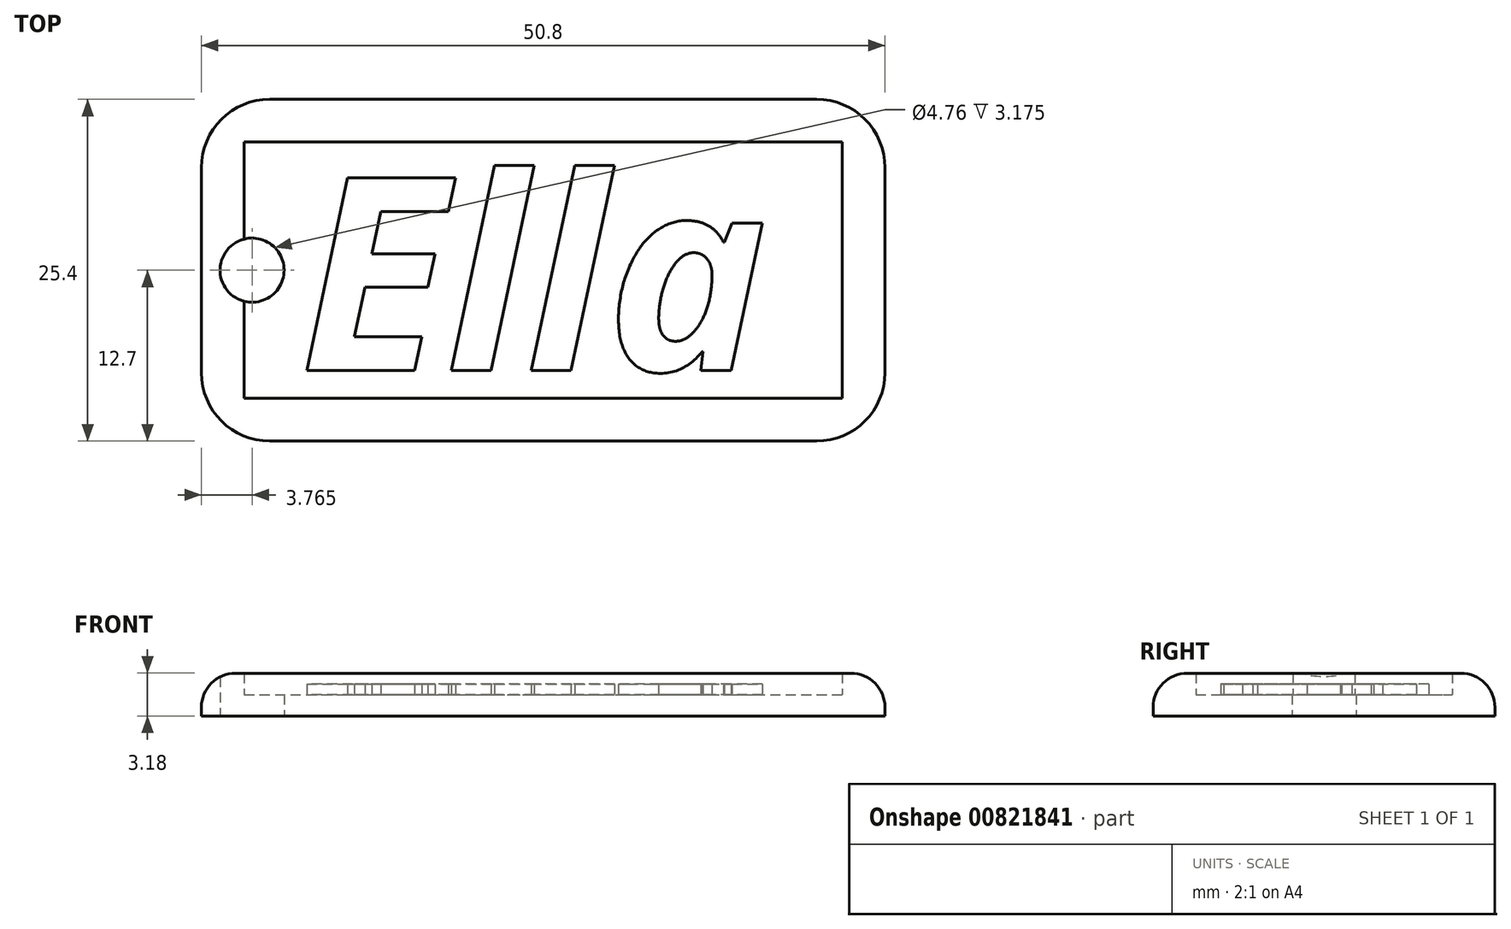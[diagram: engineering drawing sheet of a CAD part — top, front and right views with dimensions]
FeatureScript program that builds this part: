
annotation { "Feature Type Name" : "Feature", "Feature Type Description" : "" }
export const myFeature = defineFeature(function(context is Context, id is Id, definition is map)
    precondition{}
    {
        {
            var Q0;
            Q0=qCreatedBy(makeId("Top.planeOp"),FACE);
            var sketch = newSketch(context, id + "F0", { "sketchPlane" : qUnion([Q0])});
            skLineSegment(sketch, "E0.bottom", {"start": v(0, 0) * mm, "end": v(50.8, 0) * mm});
            skLineSegment(sketch, "E0.top", {"start": v(0, 25.4) * mm, "end": v(50.8, 25.4) * mm});
            skLineSegment(sketch, "E0.left", {"start": v(0, 0) * mm, "end": v(0, 25.4) * mm});
            skLineSegment(sketch, "E0.right", {"start": v(50.8, 0) * mm, "end": v(50.8, 25.4) * mm});
            skCircle(sketch, "E1", {"center": v(3.76, 12.7) * mm, "radius": 2.38 * mm});
            skPoint(sketch, "E1.centerSnap0", {"position": v(0, 12.7) * mm});
            skLineSegment(sketch, "E2.0", {"start": v(3.18, 22.23) * mm, "end": v(47.62, 22.23) * mm});
            skLineSegment(sketch, "E2.1", {"start": v(3.18, 3.18) * mm, "end": v(3.18, 22.22) * mm});
            skLineSegment(sketch, "E2.2", {"start": v(3.18, 3.18) * mm, "end": v(47.62, 3.18) * mm});
            skLineSegment(sketch, "E2.3", {"start": v(47.62, 3.18) * mm, "end": v(47.62, 22.23) * mm});
            skSolve(sketch);
        }
        {
            var Q0;
            {var subQ1=sQuery(id+"F0.wireOp",EDGE,"E2.0");Q0=makeQuery(id+"F0.imprint","IMPRINT",FACE,{"disambiguationData":[TD([[makeQuery(id+"F0.imprint","IMPRINT",EDGE,{"derivedFrom":subQ1}),-1.0]])]});}
            extrude(context, id + "F1", {"entities" : qUnion([Q0]), "depth" : 1.59 * mm, "offsetDistance" : 25.4 * mm});
        }
        {
            var Q0;
            Q0=makeQuery(id+"F0.imprint","IMPRINT",FACE,{"disambiguationData":[TD([[makeQuery(id+"F0.imprint","IMPRINT",EDGE,{"derivedFrom":sQuery(id+"F0.wireOp",EDGE,"E0.bottom")}),1.0]])]});
            extrude(context, id + "F2", {"entities" : qUnion([Q0]), "operationType" : NewBodyOperationType.ADD, "depth" : 3.17 * mm, "offsetDistance" : 25.4 * mm});
        }
        {
            var Q0;
            Q0=makeQuery(id+"F2.opExtrude","SWEPT_EDGE",EDGE,{"disambiguationData":[OSD([sQuery(id+"F0.wireOp",EDGE,"E0.bottom"),sQuery(id+"F0.wireOp",EDGE,"E0.left")])]});
            var Q1;
            Q1=makeQuery(id+"F2.opExtrude","SWEPT_EDGE",EDGE,{"disambiguationData":[OSD([sQuery(id+"F0.wireOp",EDGE,"E0.bottom"),sQuery(id+"F0.wireOp",EDGE,"E0.right")])]});
            var Q2;
            Q2=makeQuery(id+"F2.opExtrude","SWEPT_EDGE",EDGE,{"disambiguationData":[OSD([sQuery(id+"F0.wireOp",EDGE,"E0.top"),sQuery(id+"F0.wireOp",EDGE,"E0.right")])]});
            var Q3;
            Q3=makeQuery(id+"F2.opExtrude","SWEPT_EDGE",EDGE,{"disambiguationData":[OSD([sQuery(id+"F0.wireOp",EDGE,"E0.top"),sQuery(id+"F0.wireOp",EDGE,"E0.left")])]});
            fillet(context, id + "F3", {"entities" : qUnion([Q0, Q1, Q2, Q3]), "radius" : 5.08 * mm, "tangentPropagation" : true, "allowEdgeOverflow" : false});
        }
        {
            var Q0;
            Q0=makeQuery(id+"F2.opExtrude","CAP_EDGE",EDGE,{"disambiguationData":[OSD([sQuery(id+"F0.wireOp",EDGE,"E0.top")])],"isStart":false});
            fillet(context, id + "F4", {"entities" : qUnion([Q0]), "radius" : 2.54 * mm, "tangentPropagation" : true, "allowEdgeOverflow" : false});
        }
        {
            var Q0;
            Q0=makeQuery(id+"F1.opExtrude","CAP_FACE",FACE,{"disambiguationData":[OSD([sQuery(id+"F0.wireOp",EDGE,"E1"),sQuery(id+"F0.wireOp",EDGE,"E2.0"),sQuery(id+"F0.wireOp",EDGE,"E2.1"),sQuery(id+"F0.wireOp",EDGE,"E2.2"),sQuery(id+"F0.wireOp",EDGE,"E2.3")])],"isStart":false});
            var sketch = newSketch(context, id + "F5", { "sketchPlane" : qUnion([Q0])});
            skText(sketch, "E3", { "text": "Ella", "fontName": "OpenSans-BoldItalic.ttf"});
            const initialGuessF5  = {"E3": [0.00732, 0.00523, 1, 0, 0.01445]};
            skSetInitialGuess(sketch, initialGuessF5);
            skSolve(sketch);
        }
        {
            var Q0;
            Q0 = qSketchRegion(id + "F5", true);
            extrude(context, id + "F6", {"entities" : qUnion([Q0]), "operationType" : NewBodyOperationType.ADD, "depth" : 0.8 * mm, "offsetDistance" : 25.4 * mm});
        }
    });
